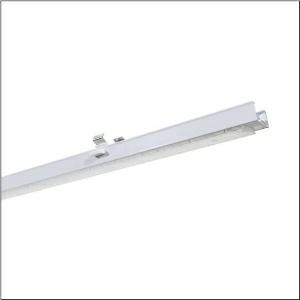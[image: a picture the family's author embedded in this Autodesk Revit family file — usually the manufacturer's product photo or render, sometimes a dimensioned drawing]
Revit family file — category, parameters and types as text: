
# Revit family: sanierungs-leuchteneinsatz_31_gen_2_51re11db49b_9f94
name_source: partatom
category: Lighting Fixtures
units: mm (PartAtom-declared; Revit-internal decimal feet)

## family parameters
Cut with Voids When Loaded = No
Host = Face
Light Source = No
Part Type = Normal
Room Calculation Point = No
Round Connector Dimension = Use Diameter
Shared = No

## types (1)
- --- (1 x LED, 8900 lm, 56 W, 4000K)
    Apparent Load = 56 VA
    CIE Flux Codes = 83 93 98 100 100
    Color Rendering = 80
    Color Temperature = 4000K
    Default Elevation = 1800 mm
    Description = Refurbishment luminaire insert Gen.2, luminaire insert, of extruded aluminium section, coated, traffic white (RAL 9016), length: 1.472mm, width: 91mm, height: 53mm, LED rated luminous flux: 8.900lm, light colour: 840, control gear: DALI 2, with system connector: socket, mains connection: 220..240V, AC, 50/60Hz, primary light control with lens, of plastic, primary optical cover: cover, of PMMA, light emission: direct distribution, protection rating (complete): IP20, insulation class (complete): insulation class I (protective earthing), certification: CE, UKCA, impact resistance: IK02, permissible ambient temperature for indoor applications: -20..+40°C, packaging unit: 1 piece
    Height = 58 mm
    Lamp = 1 x LED
    Lamp Light Flux = 8900 lm
    Lamp Power = 56 W
    Lamp count = 1
    Length = 1472 mm
    Luminous efficacy = 159 lm/W
    Manufacturer = Siteco
    ModVariant = No
    Model = 51RE11DB49B
    Mounting Place = Ceiling
    Mounting Type = Pendant
    Number of Poles = 1
    OnlyDefault = Yes
    Power Factor = 1
    Product Name = Sanierungs-Leuchteneinsatz 31 Gen.2
    Product group = luminaire insert
    ProductGroupID = 902
    Protection Class = Protection class I
    Protection Degree = IP 20
    RLX_Detail_Level = 1
    RlxData = <blob elided: 21645 chars, md5=85ac03c7>
    Socket = socket
    Standby Power = 0 W
    System Light Flux = 8900 lm
    System Power = 56 W
    Type Comments = individual setting: luminous flux: 100 % | (OFF | ON | OFF | OFF) | 1200 mA
    Type Image = l_1266702.jpg
    URL = http://relux.com
    VarID = @adj_049527
    Voltage = 0 V
    Weight = 0.00 kg
    Width = 65 mm

## geometry (parser evidence)
native form markers: Blend x4, Sweep x11
no freeform markers — native parametric forms only
